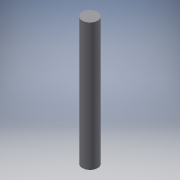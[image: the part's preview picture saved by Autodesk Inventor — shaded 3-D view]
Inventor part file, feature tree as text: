
AUTODESK INVENTOR PART (.ipt)
format: ipt  version: 2019.4 (Build 234330000, 330)  size: 89,600 bytes
history: native  units: mm
features: extrude x1, sketch x1
ambient origin geometry x8: Origin, YZ Plane, XZ Plane, XY Plane, X Axis, Y Axis, Z Axis, Center Point
bodies: Solid1 (feature_tree)
feature tree (2):
  extrude  "Extrusion1"  Depth=50.0mm TaperAngle=0.0deg
  sketch  "Sketch1"  dims[d0=6.0mm d1=50.0mm d2=0.0mm]
